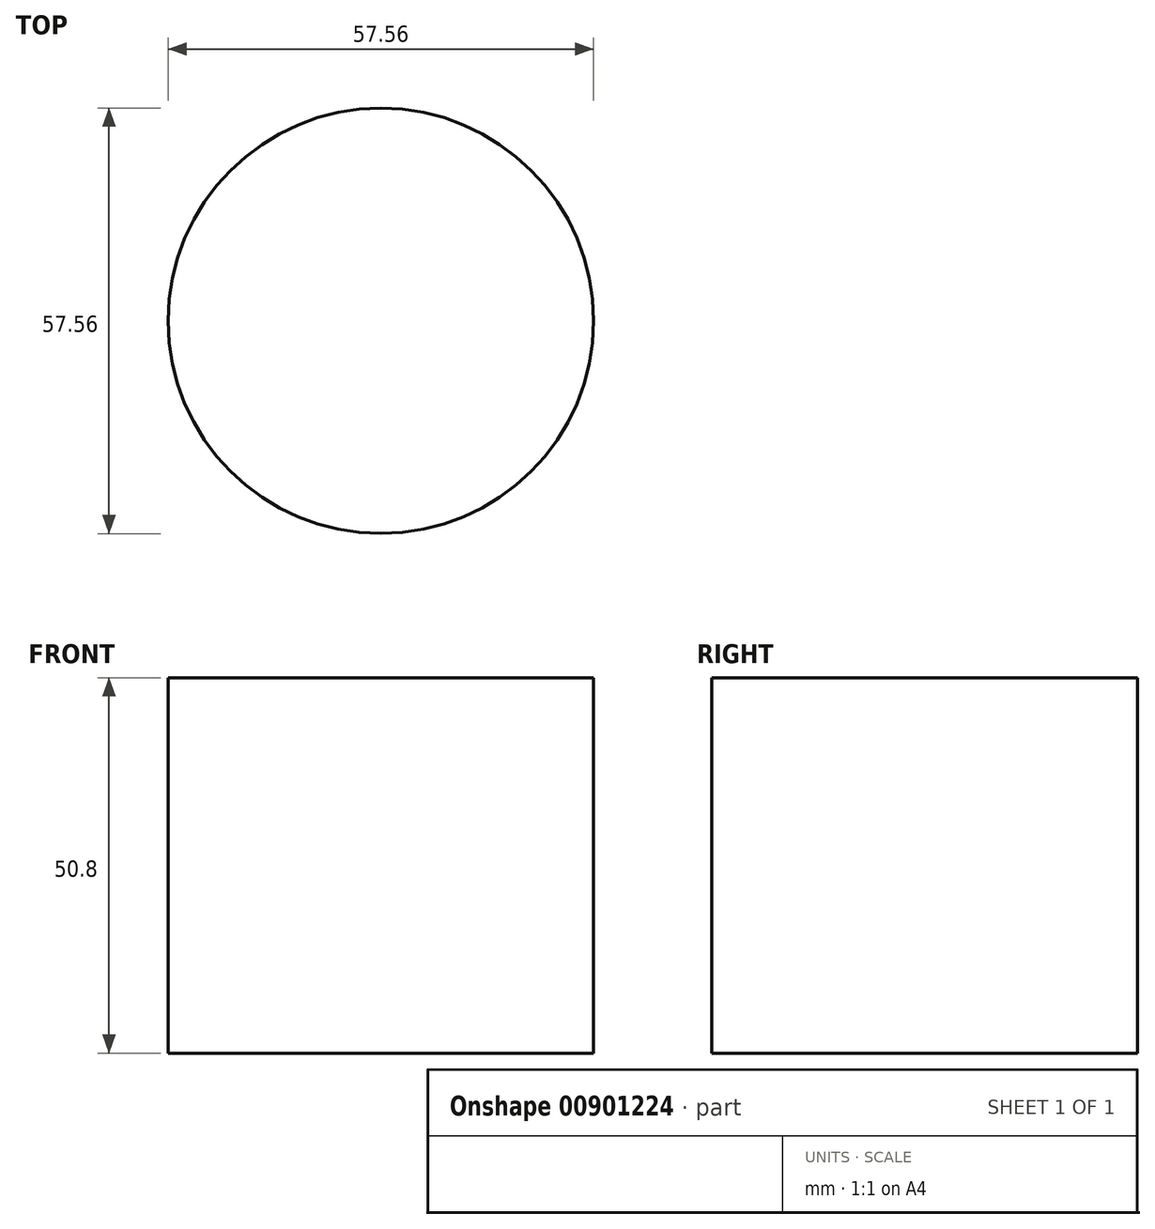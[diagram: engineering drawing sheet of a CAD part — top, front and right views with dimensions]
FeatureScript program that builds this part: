
annotation { "Feature Type Name" : "Feature", "Feature Type Description" : "" }
export const myFeature = defineFeature(function(context is Context, id is Id, definition is map)
    precondition{}
    {
        {
            var Q0;
            Q0=qCreatedBy(makeId("Top.planeOp"),FACE);
            var sketch = newSketch(context, id + "F0", { "sketchPlane" : qUnion([Q0])});
            skCircle(sketch, "E0", {"center": v(0, 0) * mm, "radius": 28.78 * mm});
            skSolve(sketch);
        }
        {
            var Q0;
            Q0 = qSketchRegion(id + "F0", true);
            extrude(context, id + "F1", {"entities" : qUnion([Q0]), "depth" : 25.4 * mm, "offsetDistance" : 25.4 * mm});
        }
        {
            var Q0;
            Q0=makeQuery(id+"F1.opExtrude","CAP_FACE",FACE,{"disambiguationData":[OSD([sQuery(id+"F0.wireOp",EDGE,"E0")])],"isStart":false});
            var sketch = newSketch(context, id + "F2", { "sketchPlane" : qUnion([Q0])});
            skSolve(sketch);
        }
        {
            var Q0;
            Q0=makeQuery(id+"F2.imprint","IMPRINT",FACE,{"disambiguationData":[TD([[makeQuery(id+"F2.imprint","IMPRINT",EDGE,{"derivedFrom":makeQuery(id+"F1.opExtrude","CAP_EDGE",EDGE,{"disambiguationData":[OSD([sQuery(id+"F0.wireOp",EDGE,"E0")])],"isStart":false})}),1.0]])]});
            extrude(context, id + "F3", {"entities" : qUnion([Q0]), "operationType" : NewBodyOperationType.ADD, "depth" : 25.4 * mm, "offsetDistance" : 25.4 * mm});
        }
    });
